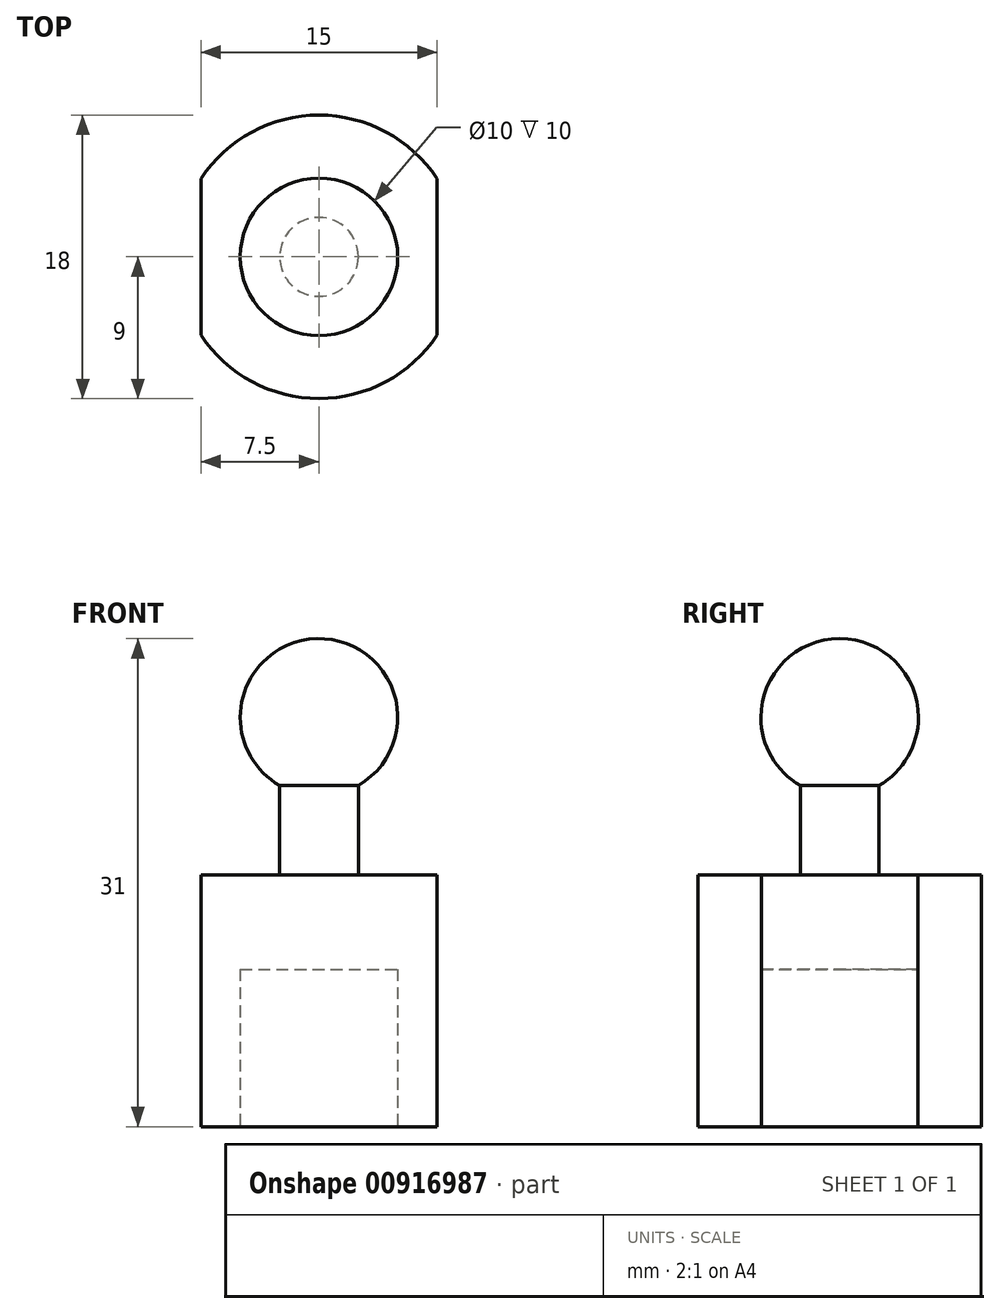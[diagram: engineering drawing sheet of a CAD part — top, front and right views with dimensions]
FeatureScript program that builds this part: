
annotation { "Feature Type Name" : "Feature", "Feature Type Description" : "" }
export const myFeature = defineFeature(function(context is Context, id is Id, definition is map)
    precondition{}
    {
        {
            var Q0;
            Q0=qCreatedBy(makeId("Top.planeOp"),FACE);
            var sketch = newSketch(context, id + "F0", { "sketchPlane" : qUnion([Q0])});
            skArc(sketch, "E0", {"start": v(-7.5, -4.97) * mm, "mid": v(0, -9) * mm, "end": v(7.5, -4.97) * mm});
            skLineSegment(sketch, "E1", {"start": v(0, 9) * mm, "end": v(0, -9) * mm, "construction": true});
            skLineSegment(sketch, "E2.0", {"start": v(-7.5, 4.97) * mm, "end": v(-7.5, -4.97) * mm});
            skLineSegment(sketch, "E3.0", {"start": v(7.5, 4.97) * mm, "end": v(7.5, -4.97) * mm});
            skArc(sketch, "E4.trimOffspring", {"start": v(7.5, 4.97) * mm, "mid": v(0, 9) * mm, "end": v(-7.5, 4.97) * mm});
            skSolve(sketch);
        }
        {
            var Q0;
            Q0=makeQuery(id+"F0.imprint","IMPRINT",FACE,{"disambiguationData":[TD([[makeQuery(id+"F0.imprint","IMPRINT",EDGE,{"derivedFrom":sQuery(id+"F0.wireOp",EDGE,"E0")}),1.0]])]});
            extrude(context, id + "F1", {"entities" : qUnion([Q0]), "depth" : 16 * mm, "offsetDistance" : 25 * mm});
        }
        {
            var Q0;
            Q0=makeQuery(id+"F1.opExtrude","CAP_FACE",FACE,{"disambiguationData":[OSD([sQuery(id+"F0.wireOp",EDGE,"E0"),sQuery(id+"F0.wireOp",EDGE,"E2.0"),sQuery(id+"F0.wireOp",EDGE,"E3.0"),sQuery(id+"F0.wireOp",EDGE,"E4.trimOffspring")])],"isStart":false});
            cPlane(context, id + "F2", {"entities" : qUnion([Q0]), "cplaneType" : CPlaneType.OFFSET, "offset" : 10 * mm, "width" : 150 * mm, "height" : 150 * mm});
        }
        {
            var Q0;
            Q0=qCreatedBy(id+"F2.planeOp",FACE);
            var sketch = newSketch(context, id + "F3", { "sketchPlane" : qUnion([Q0])});
            skArc(sketch, "E5", {"start": v(0, 5) * mm, "mid": v(-5, 0) * mm, "end": v(0, -5) * mm});
            skLineSegment(sketch, "E6", {"start": v(0, 5) * mm, "end": v(0, -5) * mm});
            skSolve(sketch);
        }
        {
            var Q0;
            Q0=makeQuery(id+"F3.imprint","IMPRINT",FACE,{"disambiguationData":[TD([[makeQuery(id+"F3.imprint","IMPRINT",EDGE,{"derivedFrom":sQuery(id+"F3.wireOp",EDGE,"E5")}),1.0]])]});
            var Q1;
            Q1=sQuery(id+"F3.wireOp",EDGE,"E6");
            revolve(context, id + "F4", {"surfaceOperationType" : NewSurfaceOperationType.NEW, "entities" : qUnion([Q0]), "axis" : qUnion([Q1]), "revolveType" : RevolveType.FULL});
        }
        {
            var Q0;
            Q0=makeQuery(id+"F1.opExtrude","CAP_FACE",FACE,{"disambiguationData":[OSD([sQuery(id+"F0.wireOp",EDGE,"E0"),sQuery(id+"F0.wireOp",EDGE,"E2.0"),sQuery(id+"F0.wireOp",EDGE,"E3.0"),sQuery(id+"F0.wireOp",EDGE,"E4.trimOffspring")])],"isStart":false});
            var sketch = newSketch(context, id + "F5", { "sketchPlane" : qUnion([Q0])});
            skCircle(sketch, "E7", {"center": v(0, 0) * mm, "radius": 2.5 * mm});
            skSolve(sketch);
        }
        {
            var Q0;
            Q0=makeQuery(id+"F5.imprint","IMPRINT",FACE,{"disambiguationData":[TD([[makeQuery(id+"F5.imprint","IMPRINT",EDGE,{"derivedFrom":sQuery(id+"F5.wireOp",EDGE,"E7")}),1.0]])]});
            extrude(context, id + "F6", {"entities" : qUnion([Q0]), "operationType" : NewBodyOperationType.ADD, "depth" : 10 * mm, "offsetDistance" : 25 * mm});
        }
        {
            var Q0;
            Q0=makeQuery(id+"F1.opExtrude","CAP_FACE",FACE,{"disambiguationData":[OSD([sQuery(id+"F0.wireOp",EDGE,"E0"),sQuery(id+"F0.wireOp",EDGE,"E2.0"),sQuery(id+"F0.wireOp",EDGE,"E3.0"),sQuery(id+"F0.wireOp",EDGE,"E4.trimOffspring")])],"isStart":true});
            var sketch = newSketch(context, id + "F7", { "sketchPlane" : qUnion([Q0])});
            skCircle(sketch, "E8", {"center": v(0, 0) * mm, "radius": 5 * mm});
            skSolve(sketch);
        }
        {
            var Q0;
            Q0 = qSketchRegion(id + "F7", true);
            extrude(context, id + "F8", {"entities" : qUnion([Q0]), "operationType" : NewBodyOperationType.REMOVE, "oppositeDirection" : true, "depth" : 10 * mm, "offsetDistance" : 25 * mm});
        }
    });
